# Revit family: NLA-1000
name_source: partatom
category: Mechanical Equipment
revit_build: Autodesk Revit MEP 2014 (Build: 20140709_2115(x64)
units: mm (PartAtom-declared; Revit-internal decimal feet)

## types (1)
- NLA-1000
    A = 914 mm
    Angle = 35.00°
    ApproximateShipmentWeight = 710 lbs
    B = 1905 mm
    BottomOfTheCylinder = 155 mm
    C = 38 mm
    D = 762 mm  [stored 2.5 ft]
    DrainAngle = 63.00°
    F = 19 mm
    G = 133 mm
    HandleAngle = 120.00°
    InnerRadius = 375 mm
    Manufacturer = Wessels Company
    MaximumOperatingPressure = 125 PSIG
    MaximumOperatingTemperature = 240°F
    Model = NLA-1000
    OuterRadius = 381 mm
    PartNumber = 22011000
    SystemConnectionAngle = 50.00°
    TankVolume = 264 Gallons
    URL = http://westank.com
    VoidLength = 191 mm

note: [stored X ft] marks values corroborated as IEEE doubles in the binary element streams (Revit-internal decimal feet)

## geometry (parser evidence)
native form markers: Sweep x3
no freeform markers — native parametric forms only
